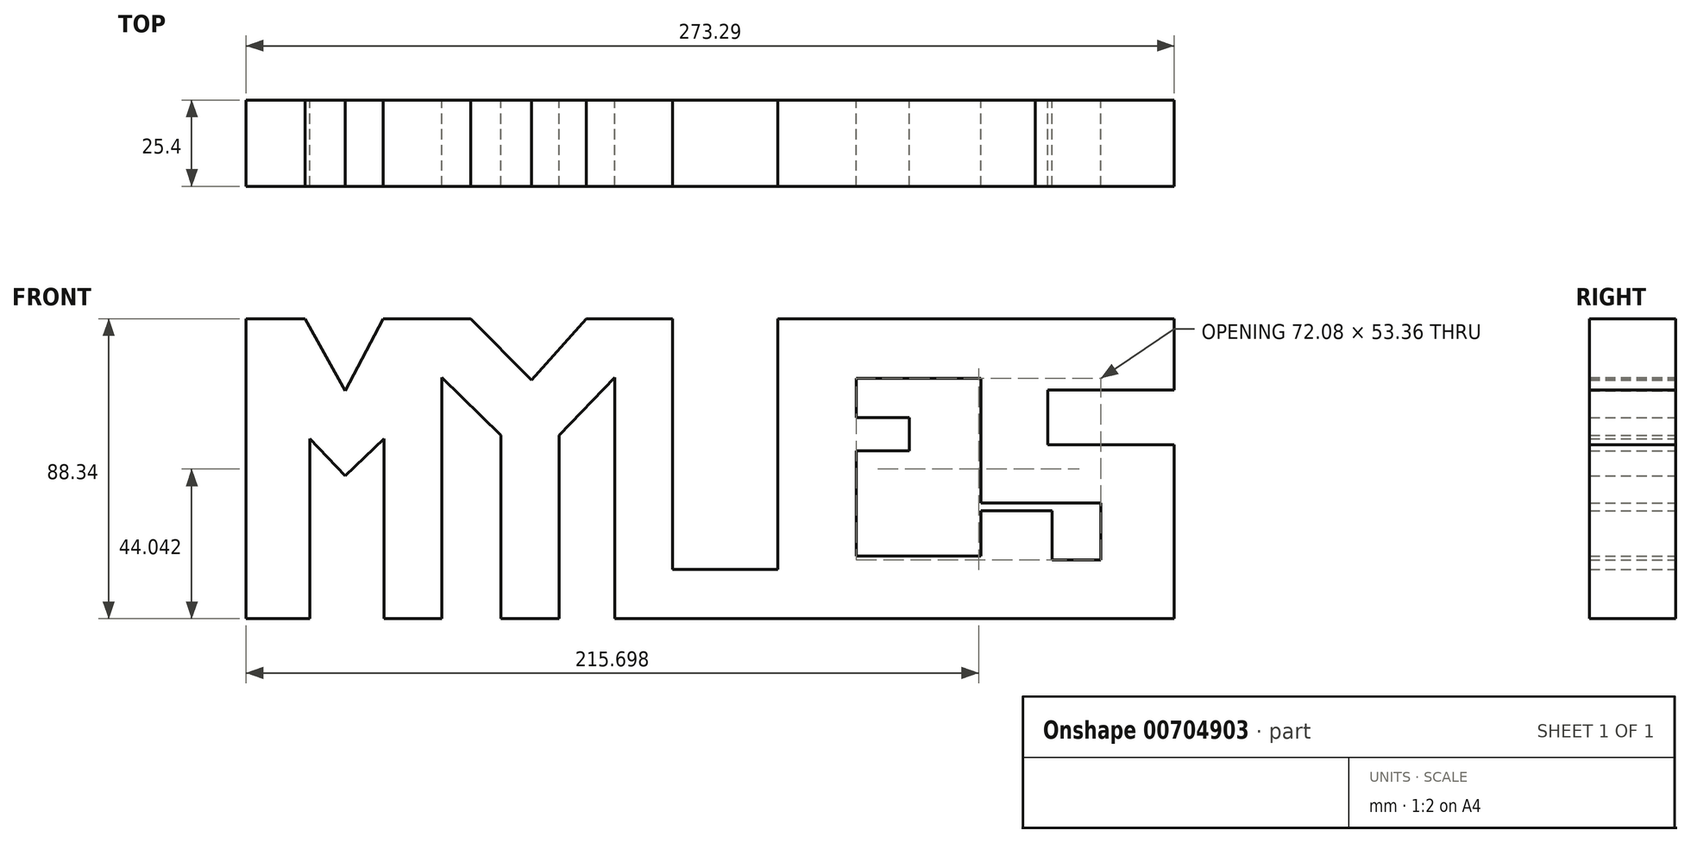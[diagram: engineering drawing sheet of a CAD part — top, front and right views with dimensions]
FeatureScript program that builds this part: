
annotation { "Feature Type Name" : "Feature", "Feature Type Description" : "" }
export const myFeature = defineFeature(function(context is Context, id is Id, definition is map)
    precondition{}
    {
        {
            var Q0;
            Q0=qCreatedBy(makeId("Front.planeOp"),FACE);
            var sketch = newSketch(context, id + "F0", { "sketchPlane" : qUnion([Q0])});
            skLineSegment(sketch, "E0.bottom", {"start": v(116.17, 44.17) * mm, "end": v(-116.17, 44.17) * mm});
            skLineSegment(sketch, "E0.top", {"start": v(116.17, -44.17) * mm, "end": v(-116.17, -44.17) * mm});
            skLineSegment(sketch, "E0.left", {"start": v(116.17, 44.17) * mm, "end": v(116.17, -44.17) * mm});
            skLineSegment(sketch, "E0.right", {"start": v(-116.17, 44.17) * mm, "end": v(-116.17, -44.17) * mm});
            skPoint(sketch, "E0.middle", {"position": v(0, 0) * mm});
            skLineSegment(sketch, "E1", {"start": v(-58.57, 44.17) * mm, "end": v(-58.57, -44.17) * mm});
            skLineSegment(sketch, "E2", {"start": v(-75.86, 44.17) * mm, "end": v(-87.06, 22.88) * mm});
            skLineSegment(sketch, "E3", {"start": v(-87.06, 22.88) * mm, "end": v(-98.83, 44.17) * mm});
            skLineSegment(sketch, "E4", {"start": v(-75.55, -44.17) * mm, "end": v(-75.55, 8.78) * mm});
            skLineSegment(sketch, "E5", {"start": v(-75.55, 8.78) * mm, "end": v(-87.06, -2.16) * mm});
            skLineSegment(sketch, "E6", {"start": v(-87.06, -2.16) * mm, "end": v(-97.45, 8.78) * mm});
            skLineSegment(sketch, "E7", {"start": v(-97.45, 8.78) * mm, "end": v(-97.45, -44.17) * mm});
            skLineSegment(sketch, "E8", {"start": v(-7.57, 44.17) * mm, "end": v(-7.57, -44.17) * mm});
            skLineSegment(sketch, "E9", {"start": v(-7.57, 26.8) * mm, "end": v(-23.98, 9.88) * mm});
            skLineSegment(sketch, "E10", {"start": v(-23.98, 9.88) * mm, "end": v(-23.98, -44.17) * mm});
            skLineSegment(sketch, "E11", {"start": v(-58.57, 26.8) * mm, "end": v(-41.1, 9.88) * mm});
            skLineSegment(sketch, "E12", {"start": v(-41.1, 9.88) * mm, "end": v(-41.1, -44.17) * mm});
            skLineSegment(sketch, "E13", {"start": v(-32.2, 26.04) * mm, "end": v(-16.04, 44.17) * mm});
            skLineSegment(sketch, "E14", {"start": v(-32.2, 26.04) * mm, "end": v(-50.09, 44.17) * mm});
            skLineSegment(sketch, "E15", {"start": v(40.4, 44.17) * mm, "end": v(40.4, -44.17) * mm});
            skLineSegment(sketch, "E16", {"start": v(9.36, 44.17) * mm, "end": v(9.36, -29.63) * mm});
            skLineSegment(sketch, "E17", {"start": v(9.36, -29.63) * mm, "end": v(40.4, -29.63) * mm});
            skLineSegment(sketch, "E18.bottom", {"start": v(180.86, 44.11) * mm, "end": v(51.47, 44.11) * mm});
            skLineSegment(sketch, "E18.top", {"start": v(180.86, -44.11) * mm, "end": v(51.47, -44.11) * mm});
            skLineSegment(sketch, "E18.left", {"start": v(180.86, 44.11) * mm, "end": v(180.86, -44.11) * mm});
            skPoint(sketch, "E18.middle", {"position": v(116.17, 0) * mm});
            skLineSegment(sketch, "E19", {"start": v(100.17, 44.11) * mm, "end": v(100.17, -44.11) * mm});
            skLineSegment(sketch, "E20", {"start": v(100.17, 26.55) * mm, "end": v(63.49, 26.55) * mm});
            skLineSegment(sketch, "E21", {"start": v(63.49, 26.55) * mm, "end": v(63.49, 15) * mm});
            skLineSegment(sketch, "E22", {"start": v(63.49, 15) * mm, "end": v(79.13, 15) * mm});
            skLineSegment(sketch, "E23", {"start": v(79.13, 15) * mm, "end": v(79.13, 5.26) * mm});
            skLineSegment(sketch, "E24", {"start": v(79.13, 5.26) * mm, "end": v(63.49, 5.26) * mm});
            skLineSegment(sketch, "E25", {"start": v(63.49, 5.26) * mm, "end": v(63.49, -25.78) * mm});
            skLineSegment(sketch, "E26", {"start": v(63.49, -25.78) * mm, "end": v(100.17, -25.78) * mm});
            skLineSegment(sketch, "E27", {"start": v(157.12, 44.11) * mm, "end": v(157.12, -44.11) * mm});
            skLineSegment(sketch, "E28", {"start": v(157.12, 23.21) * mm, "end": v(119.92, 23.21) * mm});
            skLineSegment(sketch, "E29", {"start": v(119.92, 23.21) * mm, "end": v(119.92, 7.05) * mm});
            skLineSegment(sketch, "E30", {"start": v(119.92, 7.05) * mm, "end": v(157.12, 7.05) * mm});
            skLineSegment(sketch, "E31", {"start": v(100.17, -12.44) * mm, "end": v(121.2, -12.44) * mm});
            skLineSegment(sketch, "E32", {"start": v(121.2, -12.44) * mm, "end": v(121.2, -26.8) * mm});
            skLineSegment(sketch, "E33", {"start": v(121.2, -26.8) * mm, "end": v(135.57, -26.8) * mm});
            skLineSegment(sketch, "E34", {"start": v(135.57, -26.8) * mm, "end": v(135.57, -10.13) * mm});
            skLineSegment(sketch, "E35", {"start": v(135.57, -10.13) * mm, "end": v(100.17, -10.13) * mm});
            skSolve(sketch);
        }
        {
            var Q0;
            {var subQ3=sQuery(id+"F0.wireOp",EDGE,"E0.right");Q0=makeQuery(id+"F0.imprint","IMPRINT",FACE,{"disambiguationData":[TD([[makeQuery(id+"F0.imprint","IMPRINT",EDGE,{"derivedFrom":subQ3}),1.0]])]});}
            var Q1;
            {var subQ5=sQuery(id+"F0.wireOp",EDGE,"E9");Q1=makeQuery(id+"F0.imprint","IMPRINT",FACE,{"disambiguationData":[TD([[makeQuery(id+"F0.imprint","IMPRINT",EDGE,{"derivedFrom":subQ5}),-1.0]])]});}
            var Q2;
            {var subQ9=sQuery(id+"F0.wireOp",EDGE,"E16");Q2=makeQuery(id+"F0.imprint","IMPRINT",FACE,{"disambiguationData":[TD([[makeQuery(id+"F0.imprint","IMPRINT",EDGE,{"derivedFrom":subQ9}),-1.0]])]});}
            var Q3;
            {var subQ16=sQuery(id+"F0.wireOp",EDGE,"E20");Q3=makeQuery(id+"F0.imprint","IMPRINT",FACE,{"disambiguationData":[TD([[makeQuery(id+"F0.imprint","IMPRINT",EDGE,{"derivedFrom":subQ16}),-1.0]])]});}
            var Q4;
            {var subQ6=sQuery(id+"F0.wireOp",EDGE,"E28");Q4=makeQuery(id+"F0.imprint","IMPRINT",FACE,{"disambiguationData":[TD([[makeQuery(id+"F0.imprint","IMPRINT",EDGE,{"derivedFrom":subQ6}),-1.0]])]});}
            var Q5;
            {var subQ2=sQuery(id+"F0.wireOp",EDGE,"E0.bottom");var subQ4=sQuery(id+"F0.wireOp",EDGE,"E0.left");var subQ5=makeQuery(id+"F0.imprint","INTERSECT",VERTEX,{"derivedFrom":[subQ2,subQ4]});Q5=makeQuery(id+"F0.imprint","IMPRINT",FACE,{"disambiguationData":[TD([[makeQuery(id+"F0.imprint","IMPRINT",EDGE,{"disambiguationData":[TD([[subQ5,-1.0]])],"derivedFrom":subQ2}),1.0]])]});}
            var Q6;
            {var subQ2=sQuery(id+"F0.wireOp",EDGE,"E0.top");var subQ6=sQuery(id+"F0.wireOp",EDGE,"E0.left");var subQ7=makeQuery(id+"F0.imprint","INTERSECT",VERTEX,{"derivedFrom":[subQ2,subQ6]});Q6=makeQuery(id+"F0.imprint","IMPRINT",FACE,{"disambiguationData":[TD([[makeQuery(id+"F0.imprint","IMPRINT",EDGE,{"disambiguationData":[TD([[subQ7,-1.0]])],"derivedFrom":subQ2}),-1.0]])]});}
            var Q7;
            {var subQ4=sQuery(id+"F0.wireOp",EDGE,"E18.bottom");var subQ5=sQuery(id+"F0.wireOp",EDGE,"E0.left");var subQ6=makeQuery(id+"F0.imprint","INTERSECT",VERTEX,{"derivedFrom":[subQ5,subQ4]});Q7=makeQuery(id+"F0.imprint","IMPRINT",FACE,{"disambiguationData":[TD([[makeQuery(id+"F0.imprint","IMPRINT",EDGE,{"disambiguationData":[TD([[subQ6,-1.0]])],"derivedFrom":subQ5}),-1.0]])]});}
            var Q8;
            {var subQ1=sQuery(id+"F0.wireOp",EDGE,"E18.top");var subQ6=sQuery(id+"F0.wireOp",EDGE,"E0.left");var subQ7=makeQuery(id+"F0.imprint","INTERSECT",VERTEX,{"derivedFrom":[subQ6,subQ1]});Q8=makeQuery(id+"F0.imprint","IMPRINT",FACE,{"disambiguationData":[TD([[makeQuery(id+"F0.imprint","IMPRINT",EDGE,{"disambiguationData":[TD([[subQ7,1.0]])],"derivedFrom":subQ6}),-1.0]])]});}
            extrude(context, id + "F1", {"entities" : qUnion([Q0, Q1, Q2, Q3, Q4, Q5, Q6, Q7, Q8]), "depth" : 25.4 * mm, "offsetDistance" : 25.4 * mm});
        }
    });
